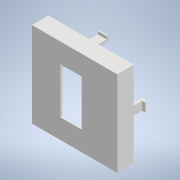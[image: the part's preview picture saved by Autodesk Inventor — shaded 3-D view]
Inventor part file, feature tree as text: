
AUTODESK INVENTOR PART (.ipt)
format: ipt  version: 2021.2 (Build 252289000, 289)  size: 225,792 bytes
history: native  units: mm
features: extrude x8, sketch x8, other x4, reference x1
ambient origin geometry x8: Origin, YZ Plane, XZ Plane, XY Plane, X Axis, Y Axis, Z Axis, Center Point
bodies: Body1 (feature_tree)
feature tree (21):
  other  "Твердое тело1"
  extrude  "Выдавливание1"  Depth=2.0mm
  extrude  "Выдавливание2"  Depth=10.0mm TaperAngle=0.0deg
  extrude  "Выдавливание3"  Depth=1.5mm TaperAngle=0.0deg
  extrude  "Выдавливание4"  Depth=4.0mm
  extrude  "Выдавливание5"  Depth=6.0mm
  extrude  "Выдавливание6"  Depth=3.0mm
  extrude  "Выдавливание7"  Depth=6.0mm
  extrude  "Выдавливание8"  Depth=4.0mm
  sketch  "Эскиз1"
  reference  "Ссылка1"
  sketch  "Эскиз2"
  sketch  "Эскиз3"
  sketch  "Эскиз4"
  sketch  "Эскиз5"
  sketch  "Эскиз6"
  sketch  "Эскиз7"
  sketch  "Эскиз8"
  parser-record x1  (decoder bookkeeping rows leaked as tree rows — omitted from the tree; the rows remain in map.json)
  other  "Сборка1.iam"
  other  "Середина 2:1"
note: 1 file-system path scrubbed to <path> (originals preserved in map.json)
